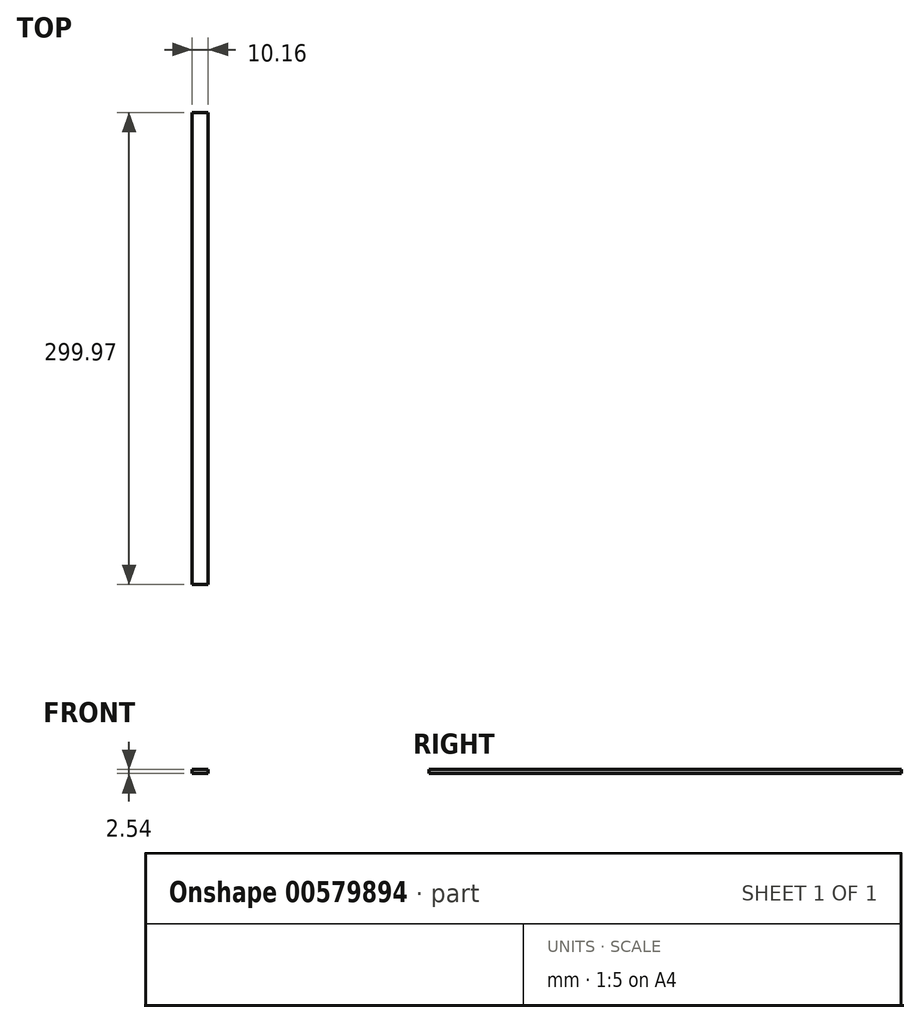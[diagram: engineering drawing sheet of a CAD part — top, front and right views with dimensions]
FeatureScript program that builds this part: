
annotation { "Feature Type Name" : "Feature", "Feature Type Description" : "" }
export const myFeature = defineFeature(function(context is Context, id is Id, definition is map)
    precondition{}
    {
        {
            var Q0;
            Q0=qCreatedBy(makeId("Top.planeOp"),FACE);
            var sketch = newSketch(context, id + "F0", { "sketchPlane" : qUnion([Q0])});
            skLineSegment(sketch, "E0.bottom", {"start": v(0, 0) * mm, "end": v(-10.16, 0) * mm});
            skLineSegment(sketch, "E0.top", {"start": v(0, -299.97) * mm, "end": v(-10.16, -299.97) * mm});
            skLineSegment(sketch, "E0.left", {"start": v(0, 0) * mm, "end": v(0, -299.97) * mm});
            skLineSegment(sketch, "E0.right", {"start": v(-10.16, 0) * mm, "end": v(-10.16, -299.97) * mm});
            skSolve(sketch);
        }
        {
            var Q0;
            Q0 = qSketchRegion(id + "F0", true);
            extrude(context, id + "F1", {"entities" : qUnion([Q0]), "depth" : 2.54 * mm, "offsetDistance" : 25.4 * mm});
        }
    });
